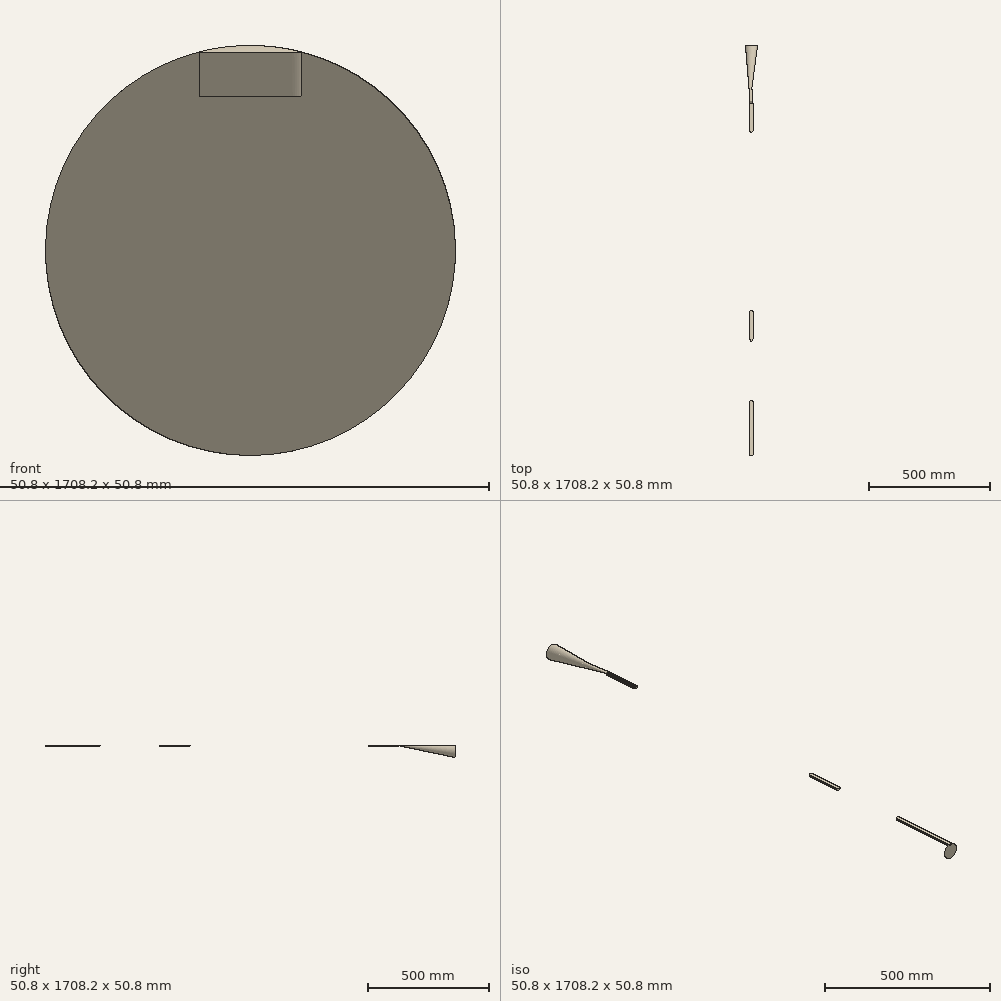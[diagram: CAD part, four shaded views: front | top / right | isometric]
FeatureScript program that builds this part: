
annotation { "Feature Type Name" : "Feature", "Feature Type Description" : "" }
export const myFeature = defineFeature(function(context is Context, id is Id, definition is map)
    precondition{}
    {
        {
            var Q0;
            Q0=qCreatedBy(makeId("Front.planeOp"),FACE);
            var sketch = newSketch(context, id + "F0", { "sketchPlane" : qUnion([Q0])});
            skCircle(sketch, "E0", {"center": v(0, 0) * mm, "radius": 25.4 * mm});
            skSolve(sketch);
        }
        {
            var Q0;
            Q0=makeQuery(id+"F0.imprint","IMPRINT",FACE,{"disambiguationData":[TD([[makeQuery(id+"F0.imprint","IMPRINT",EDGE,{"derivedFrom":sQuery(id+"F0.wireOp",EDGE,"E0")}),1.0]])]});
            extrude(context, id + "F1", {"entities" : qUnion([Q0]), "depth" : 1708.15 * mm, "offsetDistance" : 25.4 * mm});
        }
        {
            var Q0;
            Q0=qCreatedBy(makeId("Front.planeOp"),FACE);
            var sketch = newSketch(context, id + "F2", { "sketchPlane" : qUnion([Q0])});
            skPoint(sketch, "E1", {"position": v(0, 25.4) * mm});
            skSolve(sketch);
        }
        {
            var Q0;
            Q0=qCreatedBy(makeId("Top.planeOp"),FACE);
            var Q1;
            Q1=sQuery(id+"F2.wireOp",VERTEX,"E1");
            cPlane(context, id + "F3", {"entities" : qUnion([Q0, Q1]), "cplaneType" : CPlaneType.PLANE_POINT, "offset" : 25.4 * mm, "width" : 152.4 * mm, "height" : 152.4 * mm});
        }
        {
            var Q0;
            Q0=qCreatedBy(id+"F3.planeOp",FACE);
            var sketch = newSketch(context, id + "F4", { "sketchPlane" : qUnion([Q0])});
            skLineSegment(sketch, "E2", {"start": v(0, 0) * mm, "end": v(0, -1708.15) * mm, "construction": true});
            skLineSegment(sketch, "E3.bottom", {"start": v(-6.35, -241.3) * mm, "end": v(6.35, -241.3) * mm, "construction": true});
            skLineSegment(sketch, "E3.top", {"start": v(-6.35, -355.6) * mm, "end": v(6.35, -355.6) * mm, "construction": true});
            skLineSegment(sketch, "E3.left", {"start": v(-6.35, -241.3) * mm, "end": v(-6.35, -355.6) * mm});
            skLineSegment(sketch, "E3.right", {"start": v(6.35, -241.3) * mm, "end": v(6.35, -355.6) * mm});
            skPoint(sketch, "E4", {"position": v(0, -241.3) * mm});
            skPoint(sketch, "E5", {"position": v(0, -355.6) * mm});
            skArc(sketch, "E6", {"start": v(6.35, -241.3) * mm, "mid": v(0, -234.95) * mm, "end": v(-6.35, -241.3) * mm});
            skArc(sketch, "E7", {"start": v(-6.35, -355.6) * mm, "mid": v(0, -361.95) * mm, "end": v(6.35, -355.6) * mm});
            skPoint(sketch, "E8", {"position": v(0, -234.95) * mm});
            skLineSegment(sketch, "E9.bottom", {"start": v(-6.35, -1485.9) * mm, "end": v(6.35, -1485.9) * mm, "construction": true});
            skLineSegment(sketch, "E9.left", {"start": v(-6.35, -1485.9) * mm, "end": v(-6.35, -1708.15) * mm});
            skLineSegment(sketch, "E9.right", {"start": v(6.35, -1485.9) * mm, "end": v(6.35, -1708.15) * mm});
            skPoint(sketch, "E10", {"position": v(0, -1485.9) * mm});
            skArc(sketch, "E11", {"start": v(6.35, -1485.9) * mm, "mid": v(0, -1479.55) * mm, "end": v(-6.35, -1485.9) * mm});
            skPoint(sketch, "E12", {"position": v(0, -1479.55) * mm});
            skPoint(sketch, "E12.positionSnap0", {"position": v(0, -1479.55) * mm});
            skLineSegment(sketch, "E13.0", {"start": v(25.4, -1708.15) * mm, "end": v(-25.4, -1708.15) * mm, "construction": true});
            skLineSegment(sketch, "E14.bottom", {"start": v(-6.35, -1111.25) * mm, "end": v(6.35, -1111.25) * mm, "construction": true});
            skLineSegment(sketch, "E14.top", {"start": v(-6.35, -1225.55) * mm, "end": v(6.35, -1225.55) * mm, "construction": true});
            skLineSegment(sketch, "E14.left", {"start": v(-6.35, -1111.25) * mm, "end": v(-6.35, -1225.55) * mm});
            skLineSegment(sketch, "E14.right", {"start": v(6.35, -1111.25) * mm, "end": v(6.35, -1225.55) * mm});
            skArc(sketch, "E15", {"start": v(-6.35, -1225.55) * mm, "mid": v(0, -1231.9) * mm, "end": v(6.35, -1225.55) * mm});
            skArc(sketch, "E16", {"start": v(6.35, -1111.25) * mm, "mid": v(0, -1104.9) * mm, "end": v(-6.35, -1111.25) * mm});
            skPoint(sketch, "E17", {"position": v(0, -1231.9) * mm});
            skPoint(sketch, "E18", {"position": v(0, -1104.9) * mm});
            skLineSegment(sketch, "E19", {"start": v(-6.35, -1708.15) * mm, "end": v(6.35, -1708.15) * mm});
            skPoint(sketch, "E20", {"position": v(0, -361.95) * mm});
            skSolve(sketch);
        }
        {
            var Q0;
            Q0=makeQuery(id+"F4.imprint","IMPRINT",FACE,{"disambiguationData":[TD([[makeQuery(id+"F4.imprint","IMPRINT",EDGE,{"derivedFrom":sQuery(id+"F4.wireOp",EDGE,"E3.left")}),1.0]])]});
            var Q1;
            Q1=makeQuery(id+"F4.imprint","IMPRINT",FACE,{"disambiguationData":[TD([[makeQuery(id+"F4.imprint","IMPRINT",EDGE,{"derivedFrom":sQuery(id+"F4.wireOp",EDGE,"E14.left")}),1.0]])]});
            var Q2;
            Q2=makeQuery(id+"F4.imprint","IMPRINT",FACE,{"disambiguationData":[TD([[makeQuery(id+"F4.imprint","IMPRINT",EDGE,{"derivedFrom":sQuery(id+"F4.wireOp",EDGE,"E9.left")}),1.0]])]});
            extrude(context, id + "F5", {"entities" : qUnion([Q0, Q1, Q2]), "operationType" : NewBodyOperationType.REMOVE, "oppositeDirection" : true, "depth" : 6.35 * mm, "offsetDistance" : 25.4 * mm});
        }
    });
